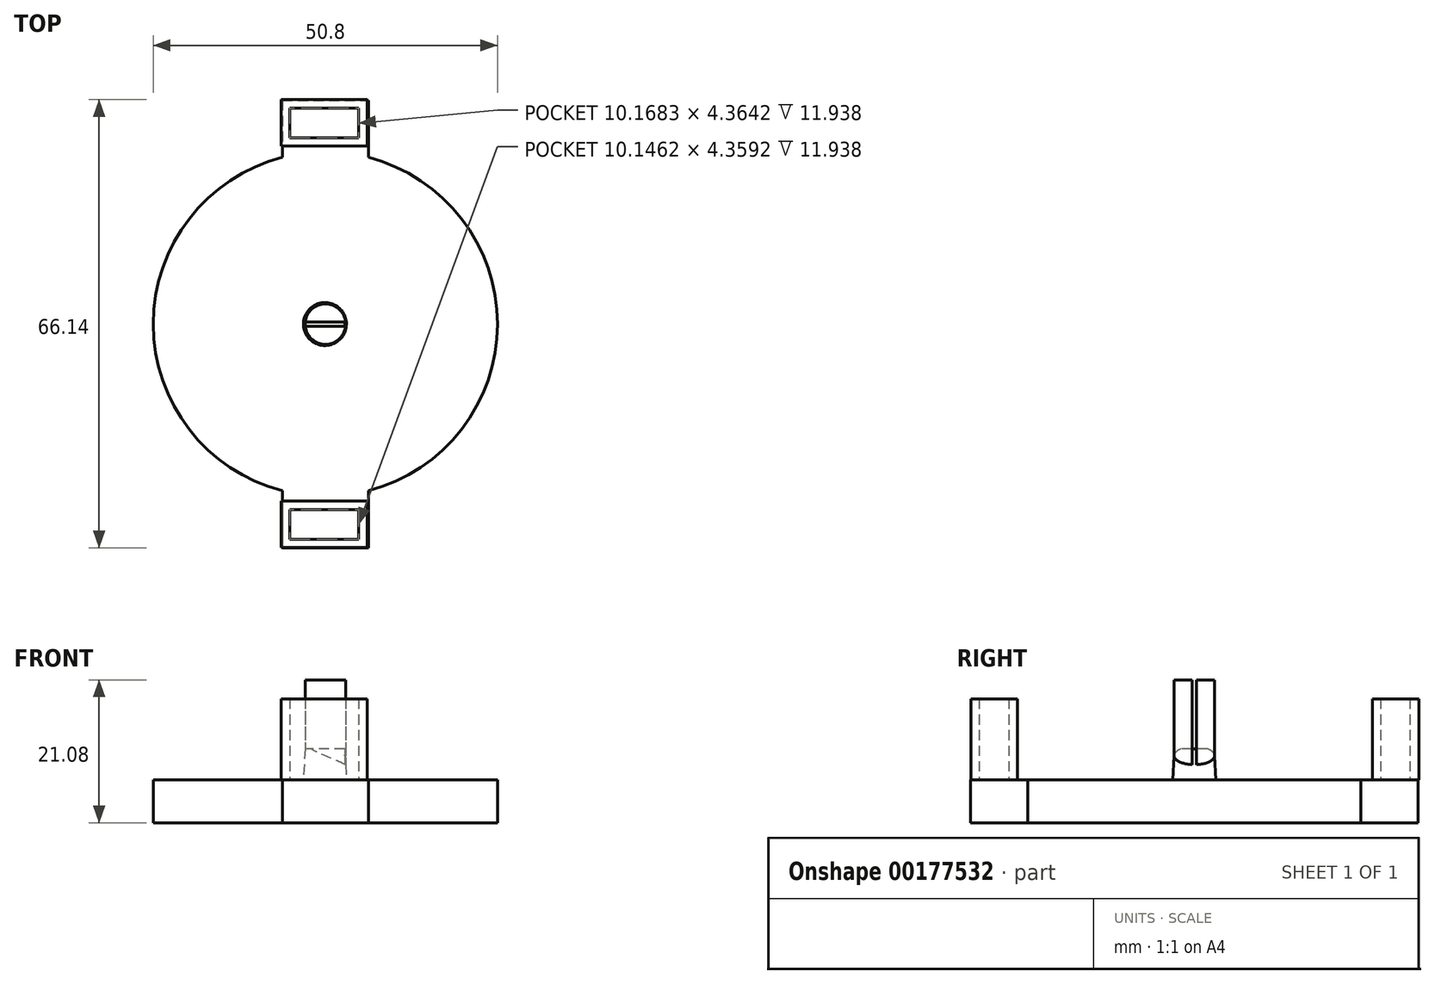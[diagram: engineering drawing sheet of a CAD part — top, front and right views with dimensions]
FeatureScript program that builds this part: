
annotation { "Feature Type Name" : "Feature", "Feature Type Description" : "" }
export const myFeature = defineFeature(function(context is Context, id is Id, definition is map)
    precondition{}
    {
        {
            var Q0;
            Q0=qCreatedBy(makeId("Top.planeOp"),FACE);
            var sketch = newSketch(context, id + "F0", { "sketchPlane" : qUnion([Q0])});
            skCircle(sketch, "E0", {"center": v(0, 0) * mm, "radius": 2.98 * mm});
            skSolve(sketch);
        }
        {
            var Q0;
            Q0=qSketchRegion(id+"F0",true);
            extrude(context, id + "F1", {"entities" : qUnion([Q0]), "depth" : 14.73 * mm});
        }
        {
            var Q0;
            Q0=qCreatedBy(makeId("Top.planeOp"),FACE);
            var sketch = newSketch(context, id + "F2", { "sketchPlane" : qUnion([Q0])});
            skLineSegment(sketch, "E1", {"start": v(-4.59, -0.78) * mm, "end": v(3.11, -0.78) * mm});
            skLineSegment(sketch, "E2", {"start": v(-4.59, -0.78) * mm, "end": v(-4.59, 0.8) * mm});
            skLineSegment(sketch, "E3", {"start": v(-4.59, 0.8) * mm, "end": v(3.11, 0.8) * mm});
            skLineSegment(sketch, "E4", {"start": v(3.11, 0.8) * mm, "end": v(3.11, -0.78) * mm});
            skLineSegment(sketch, "E5.bottom", {"start": v(4.18, 0.32) * mm, "end": v(-4.18, 0.32) * mm});
            skLineSegment(sketch, "E5.top", {"start": v(4.18, -0.32) * mm, "end": v(-4.18, -0.32) * mm});
            skLineSegment(sketch, "E5.left", {"start": v(4.18, 0.32) * mm, "end": v(4.18, -0.32) * mm});
            skLineSegment(sketch, "E5.right", {"start": v(-4.18, 0.32) * mm, "end": v(-4.18, -0.32) * mm});
            skPoint(sketch, "E5.middle", {"position": v(0, 0) * mm});
            skSolve(sketch);
        }
        {
            var Q0;
            {var subQ5=sQuery(id+"F2.wireOp",EDGE,"E5.right");Q0=makeQuery(id+"F2.imprint","IMPRINT",FACE,{"disambiguationData":[TD([[makeQuery(id+"F2.imprint","IMPRINT",EDGE,{"derivedFrom":subQ5}),1.0]])]});}
            extrude(context, id + "F3", {"entities" : qUnion([Q0]), "operationType" : NewBodyOperationType.REMOVE, "depth" : 25.4 * mm});
        }
        {
            var Q0;
            Q0=qCreatedBy(makeId("Top.planeOp"),FACE);
            var sketch = newSketch(context, id + "F4", { "sketchPlane" : qUnion([Q0])});
            skCircle(sketch, "E6", {"center": v(0, 0) * mm, "radius": 25.4 * mm});
            skSolve(sketch);
        }
        {
            var Q0;
            Q0=qSketchRegion(id+"F4",true);
            extrude(context, id + "F5", {"entities" : qUnion([Q0]), "oppositeDirection" : true, "depth" : 6.35 * mm});
        }
        {
            var Q0;
            Q0=qCreatedBy(makeId("Top.planeOp"),FACE);
            var sketch = newSketch(context, id + "F6", { "sketchPlane" : qUnion([Q0])});
            skLineSegment(sketch, "E7", {"start": v(0, 33.02) * mm, "end": v(-6.35, 33.02) * mm});
            skLineSegment(sketch, "E8", {"start": v(0, 33.02) * mm, "end": v(6.35, 33.02) * mm});
            skLineSegment(sketch, "E9", {"start": v(-6.35, 33.02) * mm, "end": v(-6.35, -33.02) * mm});
            skLineSegment(sketch, "E10", {"start": v(-6.35, -33.02) * mm, "end": v(6.35, -33.02) * mm});
            skLineSegment(sketch, "E11", {"start": v(6.35, 33.02) * mm, "end": v(6.35, -33.02) * mm});
            skSolve(sketch);
        }
        {
            var Q0;
            Q0=qSketchRegion(id+"F6",true);
            extrude(context, id + "F7", {"entities" : qUnion([Q0]), "oppositeDirection" : true, "depth" : 6.35 * mm});
        }
        {
            var Q0;
            Q0=qCreatedBy(makeId("Top.planeOp"),FACE);
            var sketch = newSketch(context, id + "F8", { "sketchPlane" : qUnion([Q0])});
            skLineSegment(sketch, "E12.bottom", {"start": v(6.2, 33.12) * mm, "end": v(-6.5, 33.12) * mm});
            skLineSegment(sketch, "E12.top", {"start": v(6.2, 26.26) * mm, "end": v(-6.5, 26.26) * mm});
            skLineSegment(sketch, "E12.left", {"start": v(6.2, 33.12) * mm, "end": v(6.2, 26.26) * mm});
            skLineSegment(sketch, "E12.right", {"start": v(-6.5, 33.12) * mm, "end": v(-6.5, 26.26) * mm});
            skPoint(sketch, "E13.firstSnap0", {"position": v(6.2, 29.69) * mm});
            skLineSegment(sketch, "E13.bottom", {"start": v(6.2, -32.96) * mm, "end": v(-6.5, -32.96) * mm});
            skLineSegment(sketch, "E13.top", {"start": v(6.2, -26.1) * mm, "end": v(-6.5, -26.1) * mm});
            skLineSegment(sketch, "E13.left", {"start": v(6.2, -32.96) * mm, "end": v(6.2, -26.1) * mm});
            skLineSegment(sketch, "E13.right", {"start": v(-6.5, -32.96) * mm, "end": v(-6.5, -26.1) * mm});
            skSolve(sketch);
        }
        {
            var Q0;
            Q0=qSketchRegion(id+"F8",true);
            extrude(context, id + "F9", {"entities" : qUnion([Q0]), "operationType" : NewBodyOperationType.ADD, "depth" : 11.94 * mm});
        }
        {
            var Q0;
            Q0=qCreatedBy(makeId("Top.planeOp"),FACE);
            var sketch = newSketch(context, id + "F10", { "sketchPlane" : qUnion([Q0])});
            skLineSegment(sketch, "E14", {"start": v(4.87, -29.43) * mm, "end": v(4.87, -31.76) * mm});
            skLineSegment(sketch, "E15", {"start": v(4.87, -31.76) * mm, "end": v(-5.28, -31.76) * mm});
            skPoint(sketch, "E16.end.orphan", {"position": v(-2.16, -31.76) * mm});
            skLineSegment(sketch, "E17", {"start": v(-5.28, -29.45) * mm, "end": v(-5.28, -31.76) * mm});
            skLineSegment(sketch, "E18", {"start": v(-1.85, -27.4) * mm, "end": v(-5.28, -27.4) * mm});
            skLineSegment(sketch, "E19", {"start": v(-5.28, -29.45) * mm, "end": v(-5.28, -27.4) * mm});
            skLineSegment(sketch, "E20", {"start": v(4.87, -29.43) * mm, "end": v(4.87, -27.4) * mm});
            skLineSegment(sketch, "E21", {"start": v(-1.85, -27.4) * mm, "end": v(4.87, -27.4) * mm});
            skSolve(sketch);
        }
        {
            var Q0;
            Q0=qSketchRegion(id+"F10",true);
            extrude(context, id + "F11", {"entities" : qUnion([Q0]), "operationType" : NewBodyOperationType.REMOVE, "depth" : 25.4 * mm});
        }
        {
            var Q0;
            Q0=qCreatedBy(makeId("Top.planeOp"),FACE);
            var sketch = newSketch(context, id + "F12", { "sketchPlane" : qUnion([Q0])});
            skLineSegment(sketch, "E22", {"start": v(-1.72, 27.48) * mm, "end": v(4.9, 27.48) * mm});
            skLineSegment(sketch, "E23", {"start": v(-1.72, 27.48) * mm, "end": v(-5.27, 27.48) * mm});
            skLineSegment(sketch, "E24", {"start": v(-5.27, 29.54) * mm, "end": v(-5.27, 27.48) * mm});
            skLineSegment(sketch, "E25", {"start": v(-0.82, 31.84) * mm, "end": v(-5.27, 31.84) * mm});
            skLineSegment(sketch, "E26", {"start": v(-5.27, 29.54) * mm, "end": v(-5.27, 31.84) * mm});
            skLineSegment(sketch, "E27", {"start": v(-0.82, 31.84) * mm, "end": v(4.9, 31.84) * mm});
            skLineSegment(sketch, "E28", {"start": v(4.9, 29.9) * mm, "end": v(4.9, 27.48) * mm});
            skLineSegment(sketch, "E29", {"start": v(4.9, 29.9) * mm, "end": v(4.9, 31.84) * mm});
            skSolve(sketch);
        }
        {
            var Q0;
            Q0=qSketchRegion(id+"F12",true);
            extrude(context, id + "F13", {"entities" : qUnion([Q0]), "operationType" : NewBodyOperationType.REMOVE, "depth" : 25.4 * mm});
        }
        {
            var Q0;
            Q0=makeQuery(id+"F5.opExtrude","CAP_FACE",FACE,{"disambiguationData":[OSD([sQuery(id+"F4.wireOp",EDGE,"E6")])],"isStart":true});
            var sketch = newSketch(context, id + "F14", { "sketchPlane" : qUnion([Q0])});
            skLineSegment(sketch, "E30.bottom", {"start": v(2.86, 0.8) * mm, "end": v(-2.88, 0.8) * mm});
            skLineSegment(sketch, "E30.top", {"start": v(2.86, -0.78) * mm, "end": v(-2.88, -0.78) * mm});
            skLineSegment(sketch, "E30.left", {"start": v(2.86, 0.8) * mm, "end": v(2.86, -0.78) * mm});
            skLineSegment(sketch, "E30.right", {"start": v(-2.88, 0.8) * mm, "end": v(-2.88, -0.78) * mm});
            skSolve(sketch);
        }
        {
            var Q0;
            Q0=qSketchRegion(id+"F14",true);
            extrude(context, id + "F15", {"entities" : qUnion([Q0]), "depth" : 2.67 * mm});
        }
        {
            var Q0;
            {var subQ0=sQuery(id+"F0.wireOp",EDGE,"E0");Q0=makeQuery(id+"F3.boolean.opBoolean","SPLIT",FACE,{"disambiguationData":[TD([makeQuery(id+"F3.opExtrude","SWEPT_FACE",FACE,{"disambiguationData":[OSD([sQuery(id+"F2.wireOp",EDGE,"E5.top")])]})])],"derivedFrom":makeQuery(id+"F1.opExtrude","CAP_FACE",FACE,{"disambiguationData":[OSD([subQ0])],"isStart":false})});}
            cPlane(context, id + "F16", {"entities" : qUnion([Q0]), "cplaneType" : CPlaneType.OFFSET, "offset" : 12.7 * mm, "oppositeDirection" : true, "width" : 152.4 * mm, "height" : 152.4 * mm});
        }
        {
            var Q0;
            Q0=qCreatedBy(id+"F16.planeOp",FACE);
            var sketch = newSketch(context, id + "F17", { "sketchPlane" : qUnion([Q0])});
            skCircle(sketch, "E31", {"center": v(-0.07, 0) * mm, "radius": 3.06 * mm});
            skSolve(sketch);
        }
        {
            var Q0;
            Q0=makeQuery(id+"F17.imprint","IMPRINT",FACE,{"disambiguationData":[TD([[makeQuery(id+"F17.imprint","IMPRINT",EDGE,{"derivedFrom":sQuery(id+"F17.wireOp",EDGE,"E31")}),1.0]])]});
            extrude(context, id + "F18", {"entities" : qUnion([Q0]), "operationType" : NewBodyOperationType.ADD, "oppositeDirection" : true, "depth" : 5.08 * mm, "hasDraft" : true, "draftAngle" : 3 * degree, "hasSecondDirection" : true, "secondDirectionOppositeDirection" : false, "secondDirectionDepth" : 2.54 * mm, "hasSecondDirectionDraft" : true, "secondDirectionDraftAngle" : 3 * degree, "secondDirectionDraftPullDirection" : true});
        }
    });
